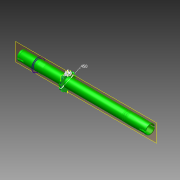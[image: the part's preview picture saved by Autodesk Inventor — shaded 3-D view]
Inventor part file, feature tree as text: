
AUTODESK INVENTOR PART (.ipt)
format: ipt  version: 2015 (Build 190159000, 159)  size: 270,848 bytes
history: native  units: in
note: dims shown in document units (in); Inventor stores cm internally (conversion verified against a paired STEP export)
features: extrude x6, sketch x5, hole x2, revolve x1, mirror x1, plane x1, pattern_circular x1
ambient origin geometry x8: Origin, YZ Plane, XZ Plane, XY Plane, X Axis, Y Axis, Z Axis, Center Point
bodies: Solid1 (feature_tree)
feature tree (17):
  revolve  "Revolution1"  [1 undecoded]
  extrude  "Extrusion1"  Depth=0.29in
  hole  "Hole1"  [1 undecoded]
  hole  "Hole2"  [1 undecoded]
  sketch  "Sketch3"  dims[d4=0.3in d5=0.1in]
  extrude  "Extrusion2"  Depth=0.05in
  extrude  "Extrusion3"  Depth=0.05in
  extrude  "Extrusion4"  Depth=0.05in
  mirror  "Mirror1"
  plane  "Work Plane2"
  sketch  "Sketch7"  dims[d8=0.3in d9=0.44in d10=0.28in d11=0.05in d12=90.0deg d13=0.04in d14=0.2in d15=1.0in d16=0.0in d17=1.0in d18=1.0in d19=0.1875in d20=0.75in d21=0.25in d22=0.25in d23=0.5635in d24=0.4375in d25=0.0in d26=1.0in d27=1.0in d28=0.1875in d29=0.75in d30=0.25in d31=0.05in d32=0.5635in d33=0.375in d34=0.0in d35=0.07in d36=0.0in d37=0.085in d38=0.0in d39=1.15in d40=0.0in d42=-1.44in d43=0.45in d44=0.025in d45=0.025in d46=0.01in d47=0.03in d48=0.05in d49=0.0in d50=0.05in d51=0.0in d52=5.1181in d53=360.0deg]
  extrude  "Extrusion5"  TaperAngle=90.0deg  [1 undecoded]
  extrude  "Extrusion6"  Depth=0.05in
  pattern_circular  "Circular Pattern1"  [2 undecoded]
  sketch  "Sketch1"  dims[d0=0.07in d1=0.4in]
  sketch  "Sketch2"  dims[d2=0.365in d3=0.29in]
  sketch  "Sketch4"  dims[d6=0.06in d7=0.3in]
note: 6 required parameter values undecoded (feature->parameter linkage not recoverable at this tier; creation-order binding heuristic only, values carry confidence <= 0.55)